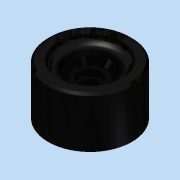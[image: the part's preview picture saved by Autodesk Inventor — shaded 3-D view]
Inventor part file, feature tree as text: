
AUTODESK INVENTOR PART (.ipt)
format: ipt  version: 2015 (Build 190159000, 159)  size: 381,952 bytes
history: native  units: in
note: dims shown in document units (in); Inventor stores cm internally (conversion verified against a paired STEP export)
features: extrude x4, chamfer x4, sketch x3, fillet x3, pattern_circular x2, revolve x1
ambient origin geometry x8: Origin, YZ Plane, XZ Plane, XY Plane, X Axis, Y Axis, Z Axis, Center Point
bodies: Solid1 (feature_tree)
feature tree (17):
  revolve  "Revolution1"  [1 undecoded]
  sketch  "Sketch3"  dims[d4=0.44in d6=0.815in]
  extrude  "Bearing Holder"  Depth=0.815in
  extrude  "Bearing Holder Lip"  Depth=0.02in
  extrude  "Spoke"  Depth=0.02in
  chamfer  "Chamfer1"  Distance=0.36in
  chamfer  "Chamfer2"  Angle=90.0deg  [1 undecoded]
  fillet  "Fillet1"  Radius=1.14in
  pattern_circular  "Spoke Pattern"  [2 undecoded]
  extrude  "Nib"  Depth=0.02in
  fillet  "Fillet2"  Radius=0.1in
  fillet  "Fillet3"  Radius=0.296in
  pattern_circular  "Nib Pattern"  [2 undecoded]
  chamfer  "Wheel Inner Chamfer"  Distance=0.296in
  chamfer  "Wheel Outer Chamfer"  Distance=0.168in Angle=45.0deg
  sketch  "Sketch2"  dims[d0=1.6339in d2=0.38in]
  sketch  "Sketch5"  dims[d7=0.29in d9=1.025in d10=0.2898in d11=0.36in d12=90.0deg d13=1.14in d14=0.834in d15=0.0in d17=0.865in d18=0.1in d19=0.296in d20=0.0in d21=0.15in d22=0.296in d23=0.0in d24=0.168in d25=0.18in d26=45.0deg d27=0.05in d28=2.3622in d29=360.0deg d31=0.168in d32=0.18in d33=45.0deg d34=30.0deg d35=0.09in d36=0.06in d37=0.296in d38=0.0in d39=0.05in d40=0.02in d41=2.3622in d42=360.0deg d44=0.08in d45=0.18in d46=45.0deg d47=0.08in d48=0.292in d49=45.0deg]
note: 6 required parameter values undecoded (feature->parameter linkage not recoverable at this tier; creation-order binding heuristic only, values carry confidence <= 0.55)